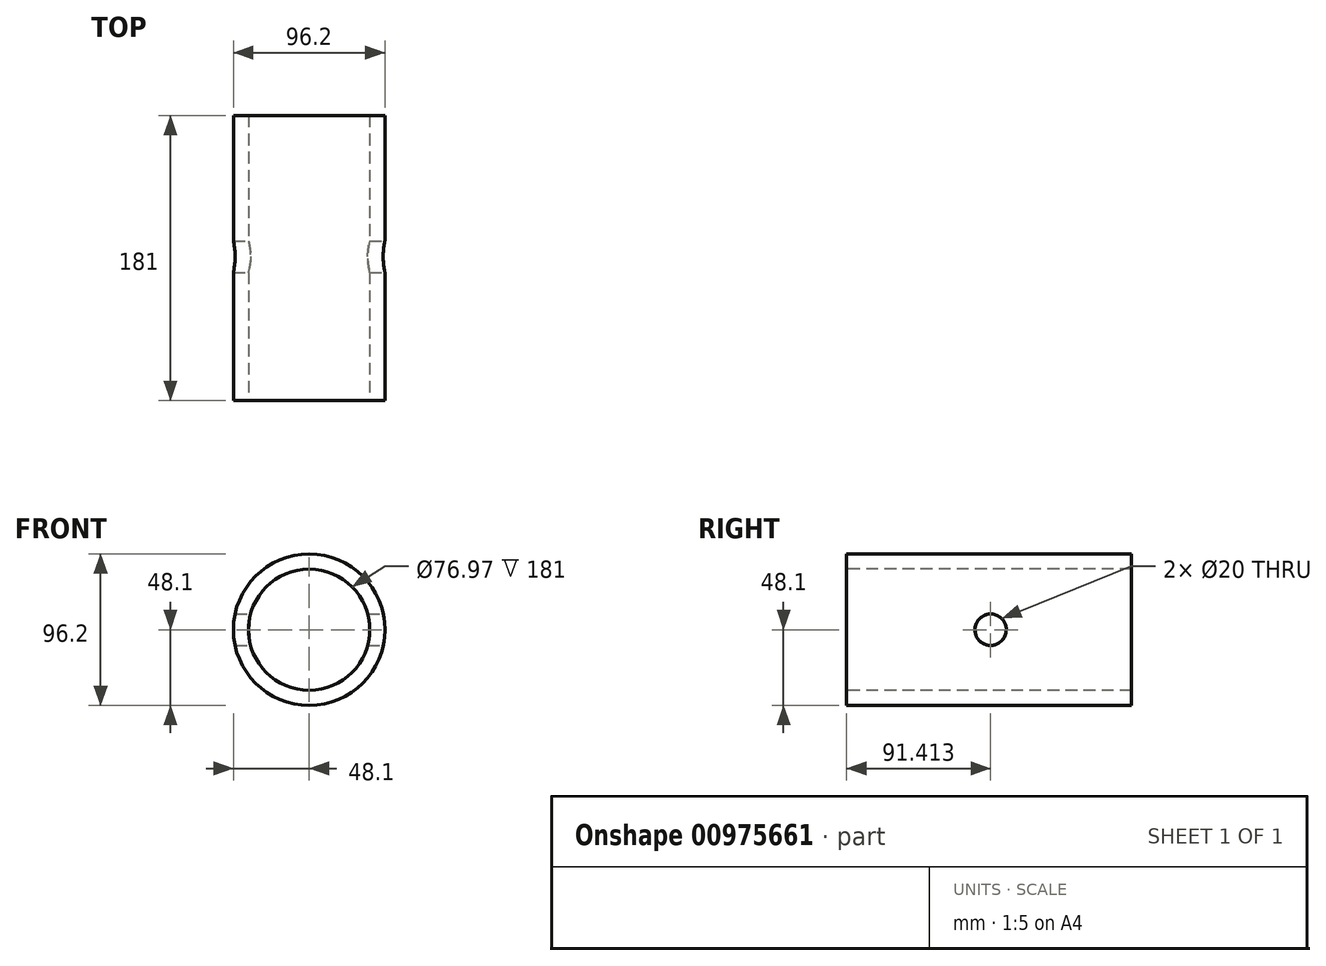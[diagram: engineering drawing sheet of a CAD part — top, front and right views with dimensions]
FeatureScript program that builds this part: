
annotation { "Feature Type Name" : "Feature", "Feature Type Description" : "" }
export const myFeature = defineFeature(function(context is Context, id is Id, definition is map)
    precondition{}
    {
        {
            var Q0;
            Q0=qCreatedBy(makeId("Front.planeOp"),FACE);
            var sketch = newSketch(context, id + "F0", { "sketchPlane" : qUnion([Q0])});
            skCircle(sketch, "E0", {"center": v(0, 0) * mm, "radius": 48.1 * mm});
            skCircle(sketch, "E1", {"center": v(0, 0) * mm, "radius": 38.49 * mm});
            skSolve(sketch);
        }
        {
            var Q0;
            Q0=makeQuery(id+"F0.imprint","IMPRINT",FACE,{"disambiguationData":[TD([[makeQuery(id+"F0.imprint","IMPRINT",EDGE,{"derivedFrom":sQuery(id+"F0.wireOp",EDGE,"E0")}),1.0]])]});
            extrude(context, id + "F1", {"entities" : qUnion([Q0]), "oppositeDirection" : true, "depth" : 181 * mm, "offsetDistance" : 25 * mm});
        }
        {
            var Q0;
            Q0=qCreatedBy(makeId("Right.planeOp"),FACE);
            var sketch = newSketch(context, id + "F2", { "sketchPlane" : qUnion([Q0])});
            skCircle(sketch, "E2", {"center": v(91.41, 0) * mm, "radius": 10 * mm});
            skSolve(sketch);
        }
        {
            var Q0;
            Q0=makeQuery(id+"F2.imprint","IMPRINT",FACE,{"disambiguationData":[TD([[makeQuery(id+"F2.imprint","IMPRINT",EDGE,{"derivedFrom":sQuery(id+"F2.wireOp",EDGE,"E2")}),1.0]])]});
            extrude(context, id + "F3", {"entities" : qUnion([Q0]), "operationType" : NewBodyOperationType.REMOVE, "endBound" : BoundingType.SYMMETRIC, "oppositeDirection" : true, "depth" : 154 * mm, "offsetDistance" : 25 * mm});
        }
    });
